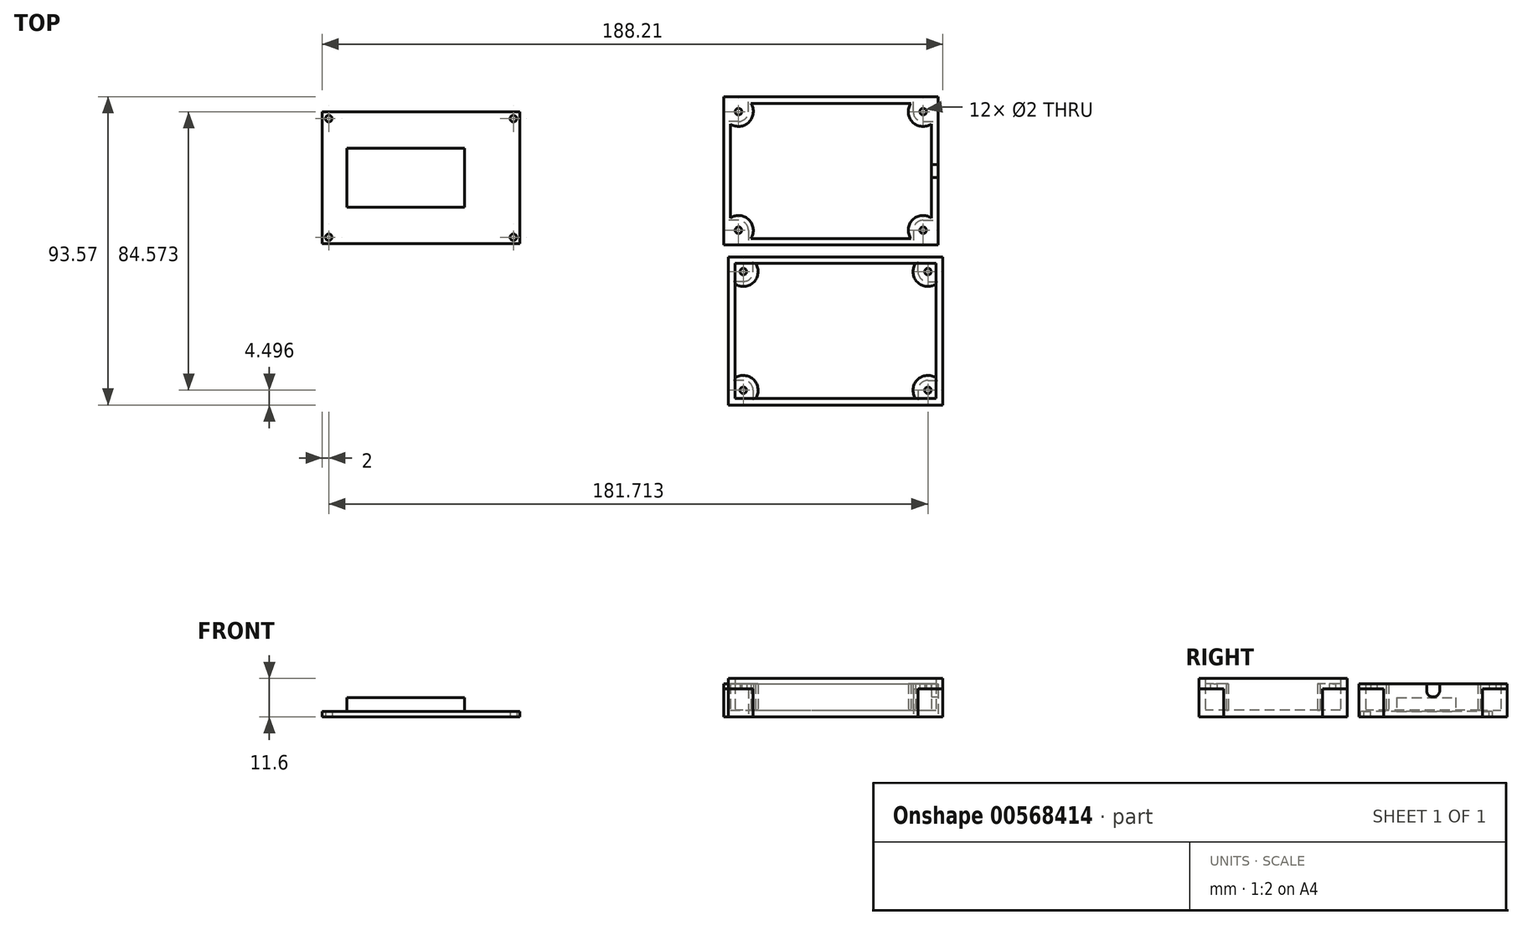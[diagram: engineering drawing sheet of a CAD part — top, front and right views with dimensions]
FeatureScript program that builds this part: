
annotation { "Feature Type Name" : "Feature", "Feature Type Description" : "" }
export const myFeature = defineFeature(function(context is Context, id is Id, definition is map)
    precondition{}
    {
        {
            var Q0;
            Q0=qCreatedBy(makeId("Top.planeOp"),FACE);
            var sketch = newSketch(context, id + "F0", { "sketchPlane" : qUnion([Q0])});
            skLineSegment(sketch, "E0.bottom", {"start": v(-101.7, 31.82) * mm, "end": v(-41.7, 31.82) * mm});
            skLineSegment(sketch, "E0.top", {"start": v(-101.7, -8.18) * mm, "end": v(-41.7, -8.18) * mm});
            skLineSegment(sketch, "E0.left", {"start": v(-101.7, 31.82) * mm, "end": v(-101.7, -8.18) * mm});
            skLineSegment(sketch, "E0.right", {"start": v(-41.7, 31.82) * mm, "end": v(-41.7, -8.18) * mm});
            skCircle(sketch, "E1", {"center": v(-99.7, 29.82) * mm, "radius": 1 * mm});
            skCircle(sketch, "E2", {"center": v(-99.7, -6.18) * mm, "radius": 1 * mm});
            skCircle(sketch, "E3", {"center": v(-43.7, 29.82) * mm, "radius": 1 * mm});
            skCircle(sketch, "E4", {"center": v(-43.7, -6.18) * mm, "radius": 1 * mm});
            skSolve(sketch);
        }
        {
            var Q0;
            Q0 = qSketchRegion(id + "F0", true);
            extrude(context, id + "F1", {"entities" : qUnion([Q0]), "depth" : 1.6 * mm, "offsetDistance" : 25.4 * mm});
        }
        {
            var Q0;
            Q0=makeQuery(id+"F1.opExtrude","CAP_FACE",FACE,{"disambiguationData":[OSD([sQuery(id+"F0.wireOp",EDGE,"E0.bottom"),sQuery(id+"F0.wireOp",EDGE,"E0.top"),sQuery(id+"F0.wireOp",EDGE,"E0.left"),sQuery(id+"F0.wireOp",EDGE,"E0.right"),sQuery(id+"F0.wireOp",EDGE,"E1"),sQuery(id+"F0.wireOp",EDGE,"E2"),sQuery(id+"F0.wireOp",EDGE,"E3"),sQuery(id+"F0.wireOp",EDGE,"E4")])],"isStart":false});
            var sketch = newSketch(context, id + "F2", { "sketchPlane" : qUnion([Q0])});
            skSolve(sketch);
        }
        {
            var Q0;
            Q0=makeQuery(id+"F2.imprint","IMPRINT",FACE,{"disambiguationData":[TD([[makeQuery(id+"F2.imprint","IMPRINT",EDGE,{"derivedFrom":makeQuery(id+"F1.opExtrude","CAP_EDGE",EDGE,{"disambiguationData":[OSD([sQuery(id+"F0.wireOp",EDGE,"E0.bottom")])],"isStart":false})}),-1.0]])]});
            var sketch = newSketch(context, id + "F3", { "sketchPlane" : qUnion([Q0])});
            skLineSegment(sketch, "E5.bottom", {"start": v(-58.5, 2.87) * mm, "end": v(-94.2, 2.87) * mm});
            skLineSegment(sketch, "E5.top", {"start": v(-58.5, 20.77) * mm, "end": v(-94.2, 20.77) * mm});
            skLineSegment(sketch, "E5.left", {"start": v(-58.5, 2.87) * mm, "end": v(-58.5, 20.77) * mm});
            skLineSegment(sketch, "E5.right", {"start": v(-94.2, 2.87) * mm, "end": v(-94.2, 20.77) * mm});
            skPoint(sketch, "E6", {"position": v(-58.5, 11.82) * mm});
            skSolve(sketch);
        }
        {
            var Q0;
            Q0=makeQuery(id+"F3.imprint","IMPRINT",FACE,{"disambiguationData":[TD([[makeQuery(id+"F3.imprint","IMPRINT",EDGE,{"derivedFrom":sQuery(id+"F3.wireOp",EDGE,"E5.bottom")}),-1.0]])]});
            extrude(context, id + "F4", {"entities" : qUnion([Q0]), "operationType" : NewBodyOperationType.ADD, "depth" : 4.2 * mm, "offsetDistance" : 25.4 * mm});
        }
        {
            var Q0;
            Q0=qCreatedBy(makeId("Top.planeOp"),FACE);
            var sketch = newSketch(context, id + "F5", { "sketchPlane" : qUnion([Q0])});
            skLineSegment(sketch, "E7.bottom", {"start": v(20.05, 36.44) * mm, "end": v(85.05, 36.44) * mm});
            skLineSegment(sketch, "E7.top", {"start": v(20.05, -8.56) * mm, "end": v(85.05, -8.56) * mm});
            skLineSegment(sketch, "E7.left", {"start": v(20.05, 36.44) * mm, "end": v(20.05, -8.56) * mm});
            skLineSegment(sketch, "E7.right", {"start": v(85.05, 36.44) * mm, "end": v(85.05, -8.56) * mm});
            skCircle(sketch, "E8", {"center": v(24.55, 31.94) * mm, "radius": 1 * mm});
            skCircle(sketch, "E9", {"center": v(24.55, -4.06) * mm, "radius": 1 * mm});
            skCircle(sketch, "E10", {"center": v(80.55, 31.94) * mm, "radius": 1 * mm});
            skCircle(sketch, "E11", {"center": v(80.55, -4.06) * mm, "radius": 1 * mm});
            skSolve(sketch);
        }
        {
            var Q0;
            Q0=makeQuery(id+"F5.imprint","IMPRINT",FACE,{"disambiguationData":[TD([[makeQuery(id+"F5.imprint","IMPRINT",EDGE,{"derivedFrom":sQuery(id+"F5.wireOp",EDGE,"E7.bottom")}),-1.0]])]});
            extrude(context, id + "F6", {"entities" : qUnion([Q0]), "depth" : 2 * mm, "offsetDistance" : 25.4 * mm});
        }
        {
            var Q0;
            Q0=makeQuery(id+"F6.opExtrude","CAP_FACE",FACE,{"disambiguationData":[OSD([sQuery(id+"F5.wireOp",EDGE,"E7.bottom"),sQuery(id+"F5.wireOp",EDGE,"E7.top"),sQuery(id+"F5.wireOp",EDGE,"E7.left"),sQuery(id+"F5.wireOp",EDGE,"E7.right"),sQuery(id+"F5.wireOp",EDGE,"E8"),sQuery(id+"F5.wireOp",EDGE,"E9"),sQuery(id+"F5.wireOp",EDGE,"E10"),sQuery(id+"F5.wireOp",EDGE,"E11")])],"isStart":false});
            var sketch = newSketch(context, id + "F7", { "sketchPlane" : qUnion([Q0])});
            skCircle(sketch, "E12", {"center": v(24.55, 31.94) * mm, "radius": 4.5 * mm});
            skCircle(sketch, "E13", {"center": v(24.55, -4.06) * mm, "radius": 4.5 * mm});
            skCircle(sketch, "E14", {"center": v(80.55, 31.94) * mm, "radius": 4.5 * mm});
            skCircle(sketch, "E15", {"center": v(80.55, -4.06) * mm, "radius": 4.5 * mm});
            skLineSegment(sketch, "E16.bottom", {"start": v(20.05, 36.44) * mm, "end": v(85.05, 36.44) * mm});
            skLineSegment(sketch, "E16.top", {"start": v(20.05, -8.56) * mm, "end": v(85.05, -8.56) * mm});
            skLineSegment(sketch, "E16.left", {"start": v(20.05, 36.44) * mm, "end": v(20.05, -8.56) * mm});
            skLineSegment(sketch, "E16.right", {"start": v(85.05, 36.44) * mm, "end": v(85.05, -8.56) * mm});
            skLineSegment(sketch, "E17.bottom", {"start": v(22.05, 34.44) * mm, "end": v(83.05, 34.44) * mm});
            skLineSegment(sketch, "E17.top", {"start": v(22.05, -6.56) * mm, "end": v(83.05, -6.56) * mm});
            skLineSegment(sketch, "E17.left", {"start": v(22.05, 34.44) * mm, "end": v(22.05, -6.56) * mm});
            skLineSegment(sketch, "E17.right", {"start": v(83.05, 34.44) * mm, "end": v(83.05, -6.56) * mm});
            skSolve(sketch);
        }
        {
            var Q0;
            Q0 = qSketchRegion(id + "F7", true);
            var Q1;
            Q1=makeQuery(id+"F7.imprint","IMPRINT",FACE,{"disambiguationData":[TD([[makeQuery(id+"F7.imprint","IMPRINT",EDGE,{"derivedFrom":makeQuery(id+"F6.opExtrude","CAP_EDGE",EDGE,{"disambiguationData":[OSD([sQuery(id+"F5.wireOp",EDGE,"E8")])],"isStart":false})}),-1.0]])]});
            var Q2;
            {var subQ0=sQuery(id+"F7.wireOp",EDGE,"E17.left");var subQ1=sQuery(id+"F7.wireOp",EDGE,"E12");var subQ2=makeQuery(id+"F7.imprint","INTERSECT",VERTEX,{"disambiguationData":[OD(0.0)],"derivedFrom":[subQ1,subQ0]});Q2=makeQuery(id+"F7.imprint","IMPRINT",FACE,{"disambiguationData":[TD([[makeQuery(id+"F7.imprint","IMPRINT",EDGE,{"disambiguationData":[TD([[subQ2,-1.0]])],"derivedFrom":subQ1}),1.0]])]});}
            var Q3;
            {var subQ0=sQuery(id+"F7.wireOp",EDGE,"E17.bottom");var subQ1=sQuery(id+"F7.wireOp",EDGE,"E12");var subQ2=makeQuery(id+"F7.imprint","INTERSECT",VERTEX,{"disambiguationData":[OD(0.0)],"derivedFrom":[subQ1,subQ0]});Q3=makeQuery(id+"F7.imprint","IMPRINT",FACE,{"disambiguationData":[TD([[makeQuery(id+"F7.imprint","IMPRINT",EDGE,{"disambiguationData":[TD([[subQ2,1.0]])],"derivedFrom":subQ1}),1.0]])]});}
            var Q4;
            {var subQ0=sQuery(id+"F7.wireOp",EDGE,"E17.bottom");var subQ1=sQuery(id+"F7.wireOp",EDGE,"E12");var subQ2=makeQuery(id+"F7.imprint","INTERSECT",VERTEX,{"disambiguationData":[OD(0.0)],"derivedFrom":[subQ1,subQ0]});Q4=makeQuery(id+"F7.imprint","IMPRINT",FACE,{"disambiguationData":[TD([[makeQuery(id+"F7.imprint","IMPRINT",EDGE,{"disambiguationData":[TD([[subQ2,-1.0]])],"derivedFrom":subQ1}),-1.0]])]});}
            var Q5;
            {var subQ0=sQuery(id+"F7.wireOp",EDGE,"E17.left");var subQ1=sQuery(id+"F7.wireOp",EDGE,"E13");var subQ2=makeQuery(id+"F7.imprint","INTERSECT",VERTEX,{"disambiguationData":[OD(0.0)],"derivedFrom":[subQ1,subQ0]});Q5=makeQuery(id+"F7.imprint","IMPRINT",FACE,{"disambiguationData":[TD([[makeQuery(id+"F7.imprint","IMPRINT",EDGE,{"disambiguationData":[TD([[subQ2,-1.0]])],"derivedFrom":subQ1}),-1.0]])]});}
            var Q6;
            {var subQ0=sQuery(id+"F7.wireOp",EDGE,"E17.top");var subQ1=sQuery(id+"F7.wireOp",EDGE,"E13");var subQ2=makeQuery(id+"F7.imprint","INTERSECT",VERTEX,{"disambiguationData":[OD(0.0)],"derivedFrom":[subQ1,subQ0]});Q6=makeQuery(id+"F7.imprint","IMPRINT",FACE,{"disambiguationData":[TD([[makeQuery(id+"F7.imprint","IMPRINT",EDGE,{"disambiguationData":[TD([[subQ2,-1.0]])],"derivedFrom":subQ1}),1.0]])]});}
            var Q7;
            {var subQ0=sQuery(id+"F7.wireOp",EDGE,"E17.left");var subQ1=sQuery(id+"F7.wireOp",EDGE,"E13");var subQ2=makeQuery(id+"F7.imprint","INTERSECT",VERTEX,{"disambiguationData":[OD(0.0)],"derivedFrom":[subQ1,subQ0]});Q7=makeQuery(id+"F7.imprint","IMPRINT",FACE,{"disambiguationData":[TD([[makeQuery(id+"F7.imprint","IMPRINT",EDGE,{"disambiguationData":[TD([[subQ2,1.0]])],"derivedFrom":subQ1}),1.0]])]});}
            var Q8;
            Q8=makeQuery(id+"F7.imprint","IMPRINT",FACE,{"disambiguationData":[TD([[makeQuery(id+"F7.imprint","IMPRINT",EDGE,{"derivedFrom":makeQuery(id+"F6.opExtrude","CAP_EDGE",EDGE,{"disambiguationData":[OSD([sQuery(id+"F5.wireOp",EDGE,"E9")])],"isStart":false})}),-1.0]])]});
            var Q9;
            {var subQ0=sQuery(id+"F7.wireOp",EDGE,"E17.top");var subQ1=sQuery(id+"F7.wireOp",EDGE,"E15");var subQ2=makeQuery(id+"F7.imprint","INTERSECT",VERTEX,{"disambiguationData":[OD(1.0)],"derivedFrom":[subQ1,subQ0]});Q9=makeQuery(id+"F7.imprint","IMPRINT",FACE,{"disambiguationData":[TD([[makeQuery(id+"F7.imprint","IMPRINT",EDGE,{"disambiguationData":[TD([[subQ2,-1.0]])],"derivedFrom":subQ1}),-1.0]])]});}
            var Q10;
            {var subQ0=sQuery(id+"F7.wireOp",EDGE,"E17.right");var subQ1=sQuery(id+"F7.wireOp",EDGE,"E15");var subQ2=makeQuery(id+"F7.imprint","INTERSECT",VERTEX,{"disambiguationData":[OD(0.0)],"derivedFrom":[subQ1,subQ0]});Q10=makeQuery(id+"F7.imprint","IMPRINT",FACE,{"disambiguationData":[TD([[makeQuery(id+"F7.imprint","IMPRINT",EDGE,{"disambiguationData":[TD([[subQ2,1.0]])],"derivedFrom":subQ1}),1.0]])]});}
            var Q11;
            {var subQ0=sQuery(id+"F7.wireOp",EDGE,"E17.top");var subQ1=sQuery(id+"F7.wireOp",EDGE,"E15");var subQ2=makeQuery(id+"F7.imprint","INTERSECT",VERTEX,{"disambiguationData":[OD(0.0)],"derivedFrom":[subQ1,subQ0]});Q11=makeQuery(id+"F7.imprint","IMPRINT",FACE,{"disambiguationData":[TD([[makeQuery(id+"F7.imprint","IMPRINT",EDGE,{"disambiguationData":[TD([[subQ2,-1.0]])],"derivedFrom":subQ1}),1.0]])]});}
            var Q12;
            Q12=makeQuery(id+"F7.imprint","IMPRINT",FACE,{"disambiguationData":[TD([[makeQuery(id+"F7.imprint","IMPRINT",EDGE,{"derivedFrom":makeQuery(id+"F6.opExtrude","CAP_EDGE",EDGE,{"disambiguationData":[OSD([sQuery(id+"F5.wireOp",EDGE,"E11")])],"isStart":false})}),-1.0]])]});
            var Q13;
            {var subQ0=sQuery(id+"F7.wireOp",EDGE,"E17.right");var subQ1=sQuery(id+"F7.wireOp",EDGE,"E14");var subQ2=makeQuery(id+"F7.imprint","INTERSECT",VERTEX,{"disambiguationData":[OD(0.0)],"derivedFrom":[subQ1,subQ0]});Q13=makeQuery(id+"F7.imprint","IMPRINT",FACE,{"disambiguationData":[TD([[makeQuery(id+"F7.imprint","IMPRINT",EDGE,{"disambiguationData":[TD([[subQ2,1.0]])],"derivedFrom":subQ1}),1.0]])]});}
            var Q14;
            {var subQ0=sQuery(id+"F7.wireOp",EDGE,"E17.bottom");var subQ1=sQuery(id+"F7.wireOp",EDGE,"E14");var subQ2=makeQuery(id+"F7.imprint","INTERSECT",VERTEX,{"disambiguationData":[OD(0.0)],"derivedFrom":[subQ1,subQ0]});Q14=makeQuery(id+"F7.imprint","IMPRINT",FACE,{"disambiguationData":[TD([[makeQuery(id+"F7.imprint","IMPRINT",EDGE,{"disambiguationData":[TD([[subQ2,1.0]])],"derivedFrom":subQ1}),-1.0]])]});}
            var Q15;
            {var subQ0=sQuery(id+"F7.wireOp",EDGE,"E17.bottom");var subQ1=sQuery(id+"F7.wireOp",EDGE,"E14");var subQ2=makeQuery(id+"F7.imprint","INTERSECT",VERTEX,{"disambiguationData":[OD(0.0)],"derivedFrom":[subQ1,subQ0]});Q15=makeQuery(id+"F7.imprint","IMPRINT",FACE,{"disambiguationData":[TD([[makeQuery(id+"F7.imprint","IMPRINT",EDGE,{"disambiguationData":[TD([[subQ2,-1.0]])],"derivedFrom":subQ1}),1.0]])]});}
            var Q16;
            Q16=makeQuery(id+"F7.imprint","IMPRINT",FACE,{"disambiguationData":[TD([[makeQuery(id+"F7.imprint","IMPRINT",EDGE,{"derivedFrom":makeQuery(id+"F6.opExtrude","CAP_EDGE",EDGE,{"disambiguationData":[OSD([sQuery(id+"F5.wireOp",EDGE,"E10")])],"isStart":false})}),-1.0]])]});
            var Q17;
            {var subQ0=sQuery(id+"F7.wireOp",EDGE,"E17.bottom");var subQ1=sQuery(id+"F7.wireOp",EDGE,"E14");var subQ2=makeQuery(id+"F7.imprint","INTERSECT",VERTEX,{"derivedFrom":[subQ1,subQ0]});Q17=makeQuery(id+"F7.imprint","IMPRINT",FACE,{"disambiguationData":[TD([[makeQuery(id+"F7.imprint","IMPRINT",EDGE,{"disambiguationData":[TD([[subQ2,1.0]])],"derivedFrom":subQ1}),1.0]])]});}
            extrude(context, id + "F8", {"entities" : qUnion([Q0, Q1, Q2, Q3, Q4, Q5, Q6, Q7, Q8, Q9, Q10, Q11, Q12, Q13, Q14, Q15, Q16, Q17]), "operationType" : NewBodyOperationType.ADD, "depth" : 8 * mm, "offsetDistance" : 25.4 * mm});
        }
        {
            var Q0;
            Q0=qCreatedBy(makeId("Top.planeOp"),FACE);
            var sketch = newSketch(context, id + "F9", { "sketchPlane" : qUnion([Q0])});
            skLineSegment(sketch, "E18.bottom", {"start": v(21.5, -12.13) * mm, "end": v(86.5, -12.13) * mm});
            skLineSegment(sketch, "E18.top", {"start": v(21.5, -57.13) * mm, "end": v(86.5, -57.13) * mm});
            skLineSegment(sketch, "E18.left", {"start": v(21.5, -12.13) * mm, "end": v(21.5, -57.13) * mm});
            skLineSegment(sketch, "E18.right", {"start": v(86.5, -12.13) * mm, "end": v(86.5, -57.13) * mm});
            skCircle(sketch, "E19", {"center": v(26, -16.63) * mm, "radius": 1 * mm});
            skCircle(sketch, "E20", {"center": v(26, -52.63) * mm, "radius": 1 * mm});
            skCircle(sketch, "E21", {"center": v(82, -16.63) * mm, "radius": 1 * mm});
            skCircle(sketch, "E22", {"center": v(82, -52.63) * mm, "radius": 1 * mm});
            skSolve(sketch);
        }
        {
            var Q0;
            Q0 = qSketchRegion(id + "F9", true);
            extrude(context, id + "F10", {"entities" : qUnion([Q0]), "depth" : 2 * mm, "offsetDistance" : 25.4 * mm});
        }
        {
            var Q0;
            Q0=makeQuery(id+"F10.opExtrude","CAP_FACE",FACE,{"disambiguationData":[OSD([sQuery(id+"F9.wireOp",EDGE,"E18.bottom"),sQuery(id+"F9.wireOp",EDGE,"E18.top"),sQuery(id+"F9.wireOp",EDGE,"E18.left"),sQuery(id+"F9.wireOp",EDGE,"E18.right"),sQuery(id+"F9.wireOp",EDGE,"E19"),sQuery(id+"F9.wireOp",EDGE,"E20"),sQuery(id+"F9.wireOp",EDGE,"E21"),sQuery(id+"F9.wireOp",EDGE,"E22")])],"isStart":false});
            var sketch = newSketch(context, id + "F11", { "sketchPlane" : qUnion([Q0])});
            skCircle(sketch, "E23", {"center": v(26, -16.63) * mm, "radius": 4.5 * mm});
            skCircle(sketch, "E24", {"center": v(82, -16.63) * mm, "radius": 4.5 * mm});
            skCircle(sketch, "E25", {"center": v(26, -52.63) * mm, "radius": 4.5 * mm});
            skCircle(sketch, "E26", {"center": v(82, -52.63) * mm, "radius": 4.5 * mm});
            skLineSegment(sketch, "E27.bottom", {"start": v(21.5, -12.13) * mm, "end": v(86.5, -12.13) * mm});
            skLineSegment(sketch, "E27.top", {"start": v(21.5, -57.13) * mm, "end": v(86.5, -57.13) * mm});
            skLineSegment(sketch, "E27.left", {"start": v(21.5, -12.13) * mm, "end": v(21.5, -57.13) * mm});
            skLineSegment(sketch, "E27.right", {"start": v(86.5, -12.13) * mm, "end": v(86.5, -57.13) * mm});
            skLineSegment(sketch, "E28.bottom", {"start": v(23.5, -14.13) * mm, "end": v(84.5, -14.13) * mm});
            skLineSegment(sketch, "E28.top", {"start": v(23.5, -55.13) * mm, "end": v(84.5, -55.13) * mm});
            skLineSegment(sketch, "E28.left", {"start": v(23.5, -14.13) * mm, "end": v(23.5, -55.13) * mm});
            skLineSegment(sketch, "E28.right", {"start": v(84.5, -14.13) * mm, "end": v(84.5, -55.13) * mm});
            skSolve(sketch);
        }
        {
            var Q0;
            Q0 = qSketchRegion(id + "F11", true);
            var Q1;
            {var subQ0=sQuery(id+"F11.wireOp",EDGE,"E28.left");var subQ1=sQuery(id+"F11.wireOp",EDGE,"E25");var subQ2=makeQuery(id+"F11.imprint","INTERSECT",VERTEX,{"disambiguationData":[OD(0.0)],"derivedFrom":[subQ1,subQ0]});Q1=makeQuery(id+"F11.imprint","IMPRINT",FACE,{"disambiguationData":[TD([[makeQuery(id+"F11.imprint","IMPRINT",EDGE,{"disambiguationData":[TD([[subQ2,-1.0]])],"derivedFrom":subQ1}),-1.0]])]});}
            var Q2;
            {var subQ0=sQuery(id+"F11.wireOp",EDGE,"E28.left");var subQ1=sQuery(id+"F11.wireOp",EDGE,"E25");var subQ2=makeQuery(id+"F11.imprint","INTERSECT",VERTEX,{"disambiguationData":[OD(0.0)],"derivedFrom":[subQ1,subQ0]});Q2=makeQuery(id+"F11.imprint","IMPRINT",FACE,{"disambiguationData":[TD([[makeQuery(id+"F11.imprint","IMPRINT",EDGE,{"disambiguationData":[TD([[subQ2,1.0]])],"derivedFrom":subQ1}),1.0]])]});}
            var Q3;
            {var subQ0=sQuery(id+"F11.wireOp",EDGE,"E28.top");var subQ1=sQuery(id+"F11.wireOp",EDGE,"E25");var subQ2=makeQuery(id+"F11.imprint","INTERSECT",VERTEX,{"disambiguationData":[OD(0.0)],"derivedFrom":[subQ1,subQ0]});Q3=makeQuery(id+"F11.imprint","IMPRINT",FACE,{"disambiguationData":[TD([[makeQuery(id+"F11.imprint","IMPRINT",EDGE,{"disambiguationData":[TD([[subQ2,-1.0]])],"derivedFrom":subQ1}),1.0]])]});}
            var Q4;
            Q4=makeQuery(id+"F11.imprint","IMPRINT",FACE,{"disambiguationData":[TD([[makeQuery(id+"F11.imprint","IMPRINT",EDGE,{"derivedFrom":makeQuery(id+"F10.opExtrude","CAP_EDGE",EDGE,{"disambiguationData":[OSD([sQuery(id+"F9.wireOp",EDGE,"E20")])],"isStart":false})}),-1.0]])]});
            var Q5;
            {var subQ0=sQuery(id+"F11.wireOp",EDGE,"E28.bottom");var subQ1=sQuery(id+"F11.wireOp",EDGE,"E23");var subQ2=makeQuery(id+"F11.imprint","INTERSECT",VERTEX,{"disambiguationData":[OD(0.0)],"derivedFrom":[subQ1,subQ0]});Q5=makeQuery(id+"F11.imprint","IMPRINT",FACE,{"disambiguationData":[TD([[makeQuery(id+"F11.imprint","IMPRINT",EDGE,{"disambiguationData":[TD([[subQ2,-1.0]])],"derivedFrom":subQ1}),-1.0]])]});}
            var Q6;
            {var subQ0=sQuery(id+"F11.wireOp",EDGE,"E28.left");var subQ1=sQuery(id+"F11.wireOp",EDGE,"E23");var subQ2=makeQuery(id+"F11.imprint","INTERSECT",VERTEX,{"disambiguationData":[OD(0.0)],"derivedFrom":[subQ1,subQ0]});Q6=makeQuery(id+"F11.imprint","IMPRINT",FACE,{"disambiguationData":[TD([[makeQuery(id+"F11.imprint","IMPRINT",EDGE,{"disambiguationData":[TD([[subQ2,-1.0]])],"derivedFrom":subQ1}),1.0]])]});}
            var Q7;
            {var subQ0=sQuery(id+"F11.wireOp",EDGE,"E28.bottom");var subQ1=sQuery(id+"F11.wireOp",EDGE,"E23");var subQ2=makeQuery(id+"F11.imprint","INTERSECT",VERTEX,{"disambiguationData":[OD(0.0)],"derivedFrom":[subQ1,subQ0]});Q7=makeQuery(id+"F11.imprint","IMPRINT",FACE,{"disambiguationData":[TD([[makeQuery(id+"F11.imprint","IMPRINT",EDGE,{"disambiguationData":[TD([[subQ2,1.0]])],"derivedFrom":subQ1}),1.0]])]});}
            var Q8;
            Q8=makeQuery(id+"F11.imprint","IMPRINT",FACE,{"disambiguationData":[TD([[makeQuery(id+"F11.imprint","IMPRINT",EDGE,{"derivedFrom":makeQuery(id+"F10.opExtrude","CAP_EDGE",EDGE,{"disambiguationData":[OSD([sQuery(id+"F9.wireOp",EDGE,"E19")])],"isStart":false})}),-1.0]])]});
            var Q9;
            {var subQ0=sQuery(id+"F11.wireOp",EDGE,"E28.bottom");var subQ1=sQuery(id+"F11.wireOp",EDGE,"E24");var subQ2=makeQuery(id+"F11.imprint","INTERSECT",VERTEX,{"disambiguationData":[OD(0.0)],"derivedFrom":[subQ1,subQ0]});Q9=makeQuery(id+"F11.imprint","IMPRINT",FACE,{"disambiguationData":[TD([[makeQuery(id+"F11.imprint","IMPRINT",EDGE,{"disambiguationData":[TD([[subQ2,1.0]])],"derivedFrom":subQ1}),-1.0]])]});}
            var Q10;
            {var subQ0=sQuery(id+"F11.wireOp",EDGE,"E28.right");var subQ1=sQuery(id+"F11.wireOp",EDGE,"E24");var subQ2=makeQuery(id+"F11.imprint","INTERSECT",VERTEX,{"disambiguationData":[OD(0.0)],"derivedFrom":[subQ1,subQ0]});Q10=makeQuery(id+"F11.imprint","IMPRINT",FACE,{"disambiguationData":[TD([[makeQuery(id+"F11.imprint","IMPRINT",EDGE,{"disambiguationData":[TD([[subQ2,1.0]])],"derivedFrom":subQ1}),1.0]])]});}
            var Q11;
            {var subQ0=sQuery(id+"F11.wireOp",EDGE,"E28.bottom");var subQ1=sQuery(id+"F11.wireOp",EDGE,"E24");var subQ2=makeQuery(id+"F11.imprint","INTERSECT",VERTEX,{"disambiguationData":[OD(0.0)],"derivedFrom":[subQ1,subQ0]});Q11=makeQuery(id+"F11.imprint","IMPRINT",FACE,{"disambiguationData":[TD([[makeQuery(id+"F11.imprint","IMPRINT",EDGE,{"disambiguationData":[TD([[subQ2,-1.0]])],"derivedFrom":subQ1}),1.0]])]});}
            var Q12;
            Q12=makeQuery(id+"F11.imprint","IMPRINT",FACE,{"disambiguationData":[TD([[makeQuery(id+"F11.imprint","IMPRINT",EDGE,{"derivedFrom":makeQuery(id+"F10.opExtrude","CAP_EDGE",EDGE,{"disambiguationData":[OSD([sQuery(id+"F9.wireOp",EDGE,"E21")])],"isStart":false})}),-1.0]])]});
            var Q13;
            {var subQ0=sQuery(id+"F11.wireOp",EDGE,"E28.top");var subQ1=sQuery(id+"F11.wireOp",EDGE,"E26");var subQ2=makeQuery(id+"F11.imprint","INTERSECT",VERTEX,{"disambiguationData":[OD(1.0)],"derivedFrom":[subQ1,subQ0]});Q13=makeQuery(id+"F11.imprint","IMPRINT",FACE,{"disambiguationData":[TD([[makeQuery(id+"F11.imprint","IMPRINT",EDGE,{"disambiguationData":[TD([[subQ2,-1.0]])],"derivedFrom":subQ1}),-1.0]])]});}
            var Q14;
            {var subQ0=sQuery(id+"F11.wireOp",EDGE,"E28.right");var subQ1=sQuery(id+"F11.wireOp",EDGE,"E26");var subQ2=makeQuery(id+"F11.imprint","INTERSECT",VERTEX,{"disambiguationData":[OD(0.0)],"derivedFrom":[subQ1,subQ0]});Q14=makeQuery(id+"F11.imprint","IMPRINT",FACE,{"disambiguationData":[TD([[makeQuery(id+"F11.imprint","IMPRINT",EDGE,{"disambiguationData":[TD([[subQ2,1.0]])],"derivedFrom":subQ1}),1.0]])]});}
            var Q15;
            {var subQ0=sQuery(id+"F11.wireOp",EDGE,"E28.top");var subQ1=sQuery(id+"F11.wireOp",EDGE,"E26");var subQ2=makeQuery(id+"F11.imprint","INTERSECT",VERTEX,{"disambiguationData":[OD(0.0)],"derivedFrom":[subQ1,subQ0]});Q15=makeQuery(id+"F11.imprint","IMPRINT",FACE,{"disambiguationData":[TD([[makeQuery(id+"F11.imprint","IMPRINT",EDGE,{"disambiguationData":[TD([[subQ2,-1.0]])],"derivedFrom":subQ1}),1.0]])]});}
            var Q16;
            Q16=makeQuery(id+"F11.imprint","IMPRINT",FACE,{"disambiguationData":[TD([[makeQuery(id+"F11.imprint","IMPRINT",EDGE,{"derivedFrom":makeQuery(id+"F10.opExtrude","CAP_EDGE",EDGE,{"disambiguationData":[OSD([sQuery(id+"F9.wireOp",EDGE,"E22")])],"isStart":false})}),-1.0]])]});
            var Q17;
            {var subQ0=sQuery(id+"F11.wireOp",EDGE,"E28.top");var subQ1=sQuery(id+"F11.wireOp",EDGE,"E25");var subQ2=makeQuery(id+"F11.imprint","INTERSECT",VERTEX,{"derivedFrom":[subQ1,subQ0]});Q17=makeQuery(id+"F11.imprint","IMPRINT",FACE,{"disambiguationData":[TD([[makeQuery(id+"F11.imprint","IMPRINT",EDGE,{"disambiguationData":[TD([[subQ2,1.0]])],"derivedFrom":subQ1}),1.0]])]});}
            var Q18;
            {var subQ0=sQuery(id+"F11.wireOp",EDGE,"E28.bottom");var subQ1=sQuery(id+"F11.wireOp",EDGE,"E23");var subQ2=makeQuery(id+"F11.imprint","INTERSECT",VERTEX,{"derivedFrom":[subQ1,subQ0]});Q18=makeQuery(id+"F11.imprint","IMPRINT",FACE,{"disambiguationData":[TD([[makeQuery(id+"F11.imprint","IMPRINT",EDGE,{"disambiguationData":[TD([[subQ2,-1.0]])],"derivedFrom":subQ1}),1.0]])]});}
            var Q19;
            {var subQ0=sQuery(id+"F11.wireOp",EDGE,"E28.bottom");var subQ1=sQuery(id+"F11.wireOp",EDGE,"E24");var subQ2=makeQuery(id+"F11.imprint","INTERSECT",VERTEX,{"derivedFrom":[subQ1,subQ0]});Q19=makeQuery(id+"F11.imprint","IMPRINT",FACE,{"disambiguationData":[TD([[makeQuery(id+"F11.imprint","IMPRINT",EDGE,{"disambiguationData":[TD([[subQ2,1.0]])],"derivedFrom":subQ1}),1.0]])]});}
            extrude(context, id + "F12", {"entities" : qUnion([Q0, Q1, Q2, Q3, Q4, Q5, Q6, Q7, Q8, Q9, Q10, Q11, Q12, Q13, Q14, Q15, Q16, Q17, Q18, Q19]), "operationType" : NewBodyOperationType.ADD, "depth" : 8 * mm, "offsetDistance" : 25.4 * mm});
        }
        {
            var Q0;
            Q0=makeQuery(id+"F12.opExtrude","CAP_FACE",FACE,{"disambiguationData":[OSD([sQuery(id+"F9.wireOp",EDGE,"E19"),sQuery(id+"F9.wireOp",EDGE,"E20"),sQuery(id+"F9.wireOp",EDGE,"E21"),sQuery(id+"F9.wireOp",EDGE,"E22"),sQuery(id+"F11.wireOp",EDGE,"E23"),sQuery(id+"F11.wireOp",EDGE,"E24"),sQuery(id+"F11.wireOp",EDGE,"E25"),sQuery(id+"F11.wireOp",EDGE,"E26"),sQuery(id+"F11.wireOp",EDGE,"E27.bottom"),sQuery(id+"F11.wireOp",EDGE,"E27.top"),sQuery(id+"F11.wireOp",EDGE,"E27.left"),sQuery(id+"F11.wireOp",EDGE,"E27.right"),sQuery(id+"F11.wireOp",EDGE,"E28.bottom"),sQuery(id+"F11.wireOp",EDGE,"E28.top"),sQuery(id+"F11.wireOp",EDGE,"E28.left"),sQuery(id+"F11.wireOp",EDGE,"E28.right")])],"isStart":false});
            var sketch = newSketch(context, id + "F13", { "sketchPlane" : qUnion([Q0])});
            skLineSegment(sketch, "E29.bottom", {"start": v(21.5, -12.13) * mm, "end": v(86.5, -12.13) * mm});
            skLineSegment(sketch, "E29.top", {"start": v(21.5, -57.13) * mm, "end": v(86.5, -57.13) * mm});
            skLineSegment(sketch, "E29.left", {"start": v(21.5, -12.13) * mm, "end": v(21.5, -57.13) * mm});
            skLineSegment(sketch, "E29.right", {"start": v(86.5, -12.13) * mm, "end": v(86.5, -57.13) * mm});
            skLineSegment(sketch, "E30.bottom", {"start": v(23.5, -14.13) * mm, "end": v(84.5, -14.13) * mm});
            skLineSegment(sketch, "E30.top", {"start": v(23.5, -55.13) * mm, "end": v(84.5, -55.13) * mm});
            skLineSegment(sketch, "E30.left", {"start": v(23.5, -14.13) * mm, "end": v(23.5, -55.13) * mm});
            skLineSegment(sketch, "E30.right", {"start": v(84.5, -14.13) * mm, "end": v(84.5, -55.13) * mm});
            skSolve(sketch);
        }
        {
            var Q0;
            Q0 = qSketchRegion(id + "F13", true);
            extrude(context, id + "F14", {"entities" : qUnion([Q0]), "operationType" : NewBodyOperationType.ADD, "depth" : 1.6 * mm, "offsetDistance" : 25.4 * mm});
        }
        {
            var Q0;
            Q0=makeQuery(id+"F10.opExtrude","CAP_FACE",FACE,{"disambiguationData":[OSD([sQuery(id+"F9.wireOp",EDGE,"E18.bottom"),sQuery(id+"F9.wireOp",EDGE,"E18.top"),sQuery(id+"F9.wireOp",EDGE,"E18.left"),sQuery(id+"F9.wireOp",EDGE,"E18.right"),sQuery(id+"F9.wireOp",EDGE,"E19"),sQuery(id+"F9.wireOp",EDGE,"E20"),sQuery(id+"F9.wireOp",EDGE,"E21"),sQuery(id+"F9.wireOp",EDGE,"E22")])],"isStart":true});
            var sketch = newSketch(context, id + "F15", { "sketchPlane" : qUnion([Q0])});
            skCircle(sketch, "E31", {"center": v(82, 52.63) * mm, "radius": 3 * mm});
            skLineSegment(sketch, "E32", {"start": v(82, 49.63) * mm, "end": v(86.5, 49.63) * mm});
            skLineSegment(sketch, "E33", {"start": v(79, 52.63) * mm, "end": v(79, 57.13) * mm});
            skCircle(sketch, "E34", {"center": v(82, 16.63) * mm, "radius": 3 * mm});
            skCircle(sketch, "E35", {"center": v(26, 52.63) * mm, "radius": 3 * mm});
            skCircle(sketch, "E36", {"center": v(26, 16.63) * mm, "radius": 3 * mm});
            skLineSegment(sketch, "E37", {"start": v(82, 19.63) * mm, "end": v(86.5, 19.63) * mm});
            skLineSegment(sketch, "E38", {"start": v(79, 16.63) * mm, "end": v(79, 12.13) * mm});
            skLineSegment(sketch, "E39", {"start": v(29, 52.63) * mm, "end": v(29, 57.13) * mm});
            skLineSegment(sketch, "E40", {"start": v(26, 49.63) * mm, "end": v(21.5, 49.63) * mm});
            skLineSegment(sketch, "E41", {"start": v(26, 19.63) * mm, "end": v(21.5, 19.63) * mm});
            skLineSegment(sketch, "E42", {"start": v(29, 16.63) * mm, "end": v(29, 12.13) * mm});
            skSolve(sketch);
        }
        {
            var Q0;
            Q0 = qSketchRegion(id + "F15", true);
            var Q1;
            {var subQ3=sQuery(id+"F15.wireOp",EDGE,"E39");Q1=makeQuery(id+"F15.imprint","IMPRINT",FACE,{"disambiguationData":[TD([[makeQuery(id+"F15.imprint","IMPRINT",EDGE,{"derivedFrom":subQ3}),1.0]])]});}
            var Q2;
            {var subQ4=sQuery(id+"F15.wireOp",EDGE,"E41");Q2=makeQuery(id+"F15.imprint","IMPRINT",FACE,{"disambiguationData":[TD([[makeQuery(id+"F15.imprint","IMPRINT",EDGE,{"derivedFrom":subQ4}),1.0]])]});}
            var Q3;
            {var subQ4=sQuery(id+"F15.wireOp",EDGE,"E37");Q3=makeQuery(id+"F15.imprint","IMPRINT",FACE,{"disambiguationData":[TD([[makeQuery(id+"F15.imprint","IMPRINT",EDGE,{"derivedFrom":subQ4}),-1.0]])]});}
            var Q4;
            {var subQ4=sQuery(id+"F15.wireOp",EDGE,"E32");Q4=makeQuery(id+"F15.imprint","IMPRINT",FACE,{"disambiguationData":[TD([[makeQuery(id+"F15.imprint","IMPRINT",EDGE,{"derivedFrom":subQ4}),1.0]])]});}
            extrude(context, id + "F16", {"entities" : qUnion([Q0, Q1, Q2, Q3, Q4]), "operationType" : NewBodyOperationType.REMOVE, "oppositeDirection" : true, "depth" : 8.5 * mm, "offsetDistance" : 25.4 * mm});
        }
        {
            var Q0;
            Q0=makeQuery(id+"F6.opExtrude","CAP_FACE",FACE,{"disambiguationData":[OSD([sQuery(id+"F5.wireOp",EDGE,"E7.bottom"),sQuery(id+"F5.wireOp",EDGE,"E7.top"),sQuery(id+"F5.wireOp",EDGE,"E7.left"),sQuery(id+"F5.wireOp",EDGE,"E7.right"),sQuery(id+"F5.wireOp",EDGE,"E8"),sQuery(id+"F5.wireOp",EDGE,"E9"),sQuery(id+"F5.wireOp",EDGE,"E10"),sQuery(id+"F5.wireOp",EDGE,"E11")])],"isStart":true});
            var sketch = newSketch(context, id + "F17", { "sketchPlane" : qUnion([Q0])});
            skCircle(sketch, "E43", {"center": v(80.55, 4.06) * mm, "radius": 3 * mm});
            skLineSegment(sketch, "E44", {"start": v(80.55, 1.06) * mm, "end": v(85.05, 1.06) * mm});
            skLineSegment(sketch, "E45", {"start": v(77.55, 4.06) * mm, "end": v(77.55, 8.56) * mm});
            skCircle(sketch, "E46", {"center": v(80.55, -31.94) * mm, "radius": 3 * mm});
            skLineSegment(sketch, "E47", {"start": v(80.55, -28.94) * mm, "end": v(85.05, -28.94) * mm});
            skLineSegment(sketch, "E48", {"start": v(77.55, -31.94) * mm, "end": v(77.55, -36.44) * mm});
            skCircle(sketch, "E49", {"center": v(24.55, 4.06) * mm, "radius": 3 * mm});
            skCircle(sketch, "E50", {"center": v(24.55, -31.94) * mm, "radius": 3 * mm});
            skLineSegment(sketch, "E51", {"start": v(27.55, 4.06) * mm, "end": v(27.55, 8.56) * mm});
            skLineSegment(sketch, "E52", {"start": v(24.55, 1.06) * mm, "end": v(20.05, 1.06) * mm});
            skLineSegment(sketch, "E53", {"start": v(27.55, -31.94) * mm, "end": v(27.55, -36.44) * mm});
            skLineSegment(sketch, "E54", {"start": v(24.55, -28.94) * mm, "end": v(20.05, -28.94) * mm});
            skSolve(sketch);
        }
        {
            var Q0;
            Q0 = qSketchRegion(id + "F17", true);
            var Q1;
            {var subQ4=sQuery(id+"F17.wireOp",EDGE,"E44");Q1=makeQuery(id+"F17.imprint","IMPRINT",FACE,{"disambiguationData":[TD([[makeQuery(id+"F17.imprint","IMPRINT",EDGE,{"derivedFrom":subQ4}),1.0]])]});}
            var Q2;
            {var subQ4=sQuery(id+"F17.wireOp",EDGE,"E47");Q2=makeQuery(id+"F17.imprint","IMPRINT",FACE,{"disambiguationData":[TD([[makeQuery(id+"F17.imprint","IMPRINT",EDGE,{"derivedFrom":subQ4}),-1.0]])]});}
            var Q3;
            {var subQ0=sQuery(id+"F17.wireOp",EDGE,"E51");Q3=makeQuery(id+"F17.imprint","IMPRINT",FACE,{"disambiguationData":[TD([[makeQuery(id+"F17.imprint","IMPRINT",EDGE,{"derivedFrom":subQ0}),1.0]])]});}
            var Q4;
            {var subQ3=sQuery(id+"F17.wireOp",EDGE,"E53");Q4=makeQuery(id+"F17.imprint","IMPRINT",FACE,{"disambiguationData":[TD([[makeQuery(id+"F17.imprint","IMPRINT",EDGE,{"derivedFrom":subQ3}),-1.0]])]});}
            extrude(context, id + "F18", {"entities" : qUnion([Q0, Q1, Q2, Q3, Q4]), "operationType" : NewBodyOperationType.REMOVE, "oppositeDirection" : true, "depth" : 8.5 * mm, "offsetDistance" : 25.4 * mm});
        }
        {
            var Q0;
            Q0=makeQuery(id+"F8.boolean.opBoolean","MERGE",FACE,{"derivedFrom":[makeQuery(id+"F6.opExtrude","SWEPT_FACE",FACE,{"disambiguationData":[OSD([sQuery(id+"F5.wireOp",EDGE,"E7.right")])]}),makeQuery(id+"F8.opExtrude","SWEPT_FACE",FACE,{"disambiguationData":[OSD([sQuery(id+"F7.wireOp",EDGE,"E16.right")])]})]});
            var sketch = newSketch(context, id + "F19", { "sketchPlane" : qUnion([Q0])});
            skCircle(sketch, "E55", {"center": v(13.94, 8) * mm, "radius": 2 * mm});
            skPoint(sketch, "E55.centerSnap0", {"position": v(13.94, 10) * mm});
            skLineSegment(sketch, "E56", {"start": v(11.94, 8) * mm, "end": v(11.94, 10) * mm});
            skLineSegment(sketch, "E57", {"start": v(15.94, 8) * mm, "end": v(15.94, 10) * mm});
            skLineSegment(sketch, "E58", {"start": v(15.94, 10) * mm, "end": v(11.94, 10) * mm});
            skSolve(sketch);
        }
        {
            var Q0;
            {var subQ0=sQuery(id+"F19.wireOp",EDGE,"E55");var subQ1=makeQuery(id+"F19.imprint","INTERSECT",VERTEX,{"derivedFrom":[subQ0,sQuery(id+"F19.wireOp",EDGE,"E57")]});Q0=makeQuery(id+"F19.imprint","IMPRINT",FACE,{"disambiguationData":[TD([[makeQuery(id+"F19.imprint","IMPRINT",EDGE,{"disambiguationData":[TD([[subQ1,-1.0]])],"derivedFrom":subQ0}),1.0]])]});}
            var Q1;
            {var subQ0=sQuery(id+"F19.wireOp",EDGE,"E57");Q1=makeQuery(id+"F19.imprint","IMPRINT",FACE,{"disambiguationData":[TD([[makeQuery(id+"F19.imprint","IMPRINT",EDGE,{"derivedFrom":subQ0}),1.0]])]});}
            var Q2;
            {var subQ0=sQuery(id+"F19.wireOp",EDGE,"E56");Q2=makeQuery(id+"F19.imprint","IMPRINT",FACE,{"disambiguationData":[TD([[makeQuery(id+"F19.imprint","IMPRINT",EDGE,{"derivedFrom":subQ0}),-1.0]])]});}
            extrude(context, id + "F20", {"entities" : qUnion([Q0, Q1, Q2]), "operationType" : NewBodyOperationType.REMOVE, "oppositeDirection" : true, "depth" : 25.4 * mm, "offsetDistance" : 25.4 * mm});
        }
    });
